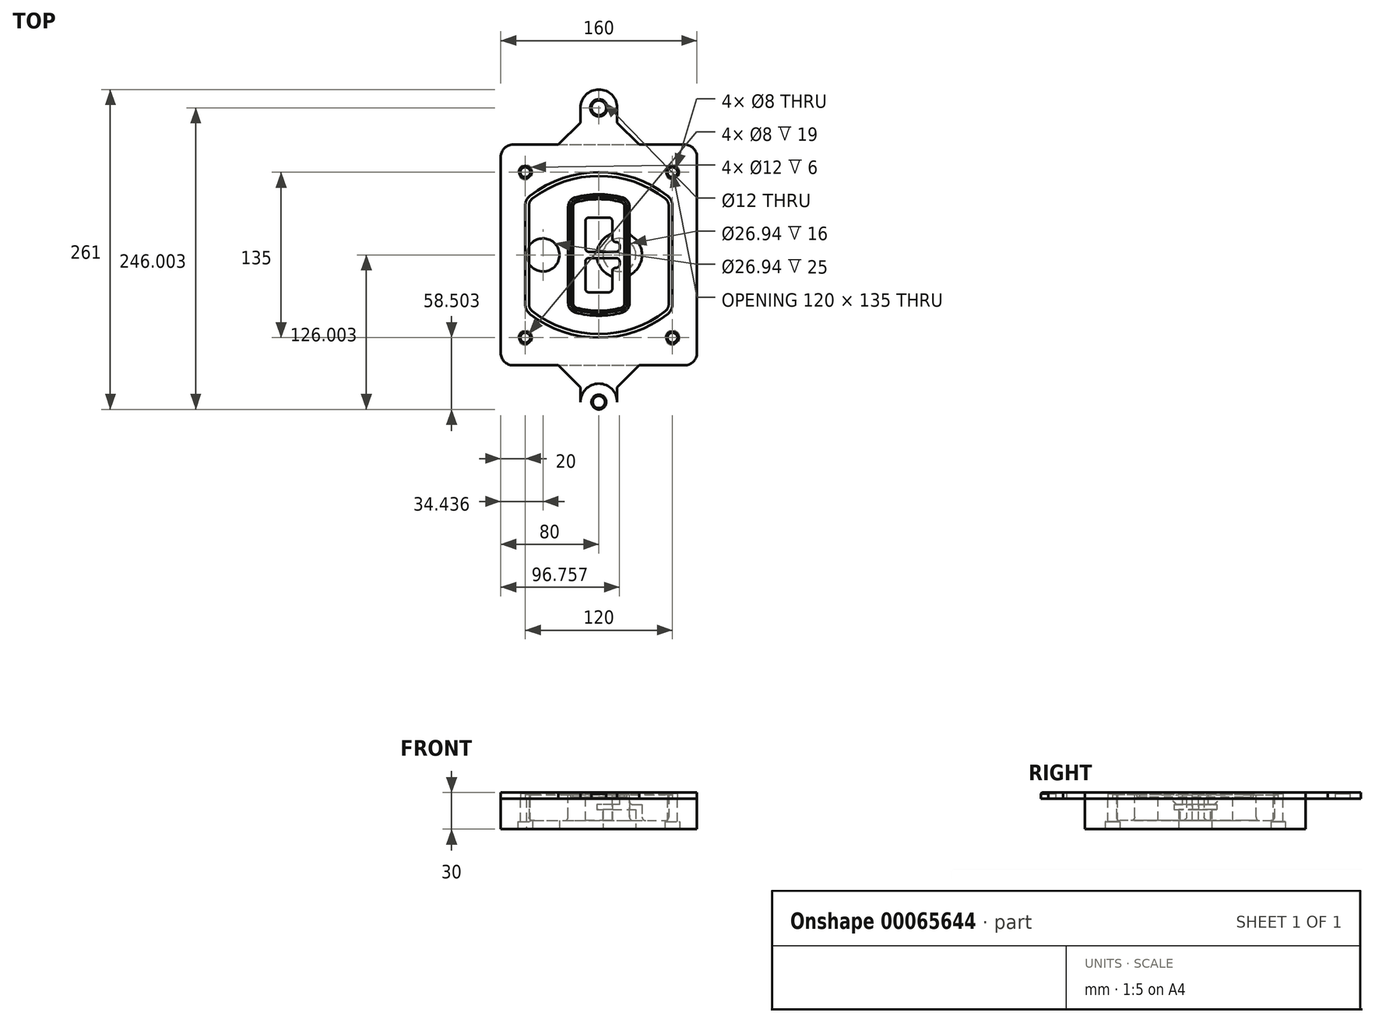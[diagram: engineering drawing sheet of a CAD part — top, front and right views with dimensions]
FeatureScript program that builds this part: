
annotation { "Feature Type Name" : "Feature", "Feature Type Description" : "" }
export const myFeature = defineFeature(function(context is Context, id is Id, definition is map)
    precondition{}
    {
        {
            var Q0;
            Q0=qCreatedBy(makeId("Top.planeOp"),FACE);
            var sketch = newSketch(context, id + "F0", { "sketchPlane" : qUnion([Q0])});
            skPoint(sketch, "E0.rect.middle", {"position": v(0, 0) * mm});
            skLineSegment(sketch, "E1.bottom", {"start": v(24.05, 28.38) * mm, "end": v(164.05, 28.38) * mm});
            skLineSegment(sketch, "E1.top", {"start": v(24.05, 208.38) * mm, "end": v(164.05, 208.38) * mm});
            skLineSegment(sketch, "E1.left", {"start": v(14.05, 38.38) * mm, "end": v(14.05, 198.38) * mm});
            skLineSegment(sketch, "E1.right", {"start": v(174.05, 38.38) * mm, "end": v(174.05, 198.38) * mm});
            skLineSegment(sketch, "E2", {"start": v(14.05, 208.38) * mm, "end": v(174.05, 28.38) * mm, "construction": true});
            skLineSegment(sketch, "E3", {"start": v(174.05, 208.38) * mm, "end": v(14.05, 28.38) * mm, "construction": true});
            skCircle(sketch, "E4", {"center": v(34.05, 185.88) * mm, "radius": 4 * mm});
            skCircle(sketch, "E5", {"center": v(154.05, 185.88) * mm, "radius": 4 * mm});
            skCircle(sketch, "E6", {"center": v(154.05, 50.88) * mm, "radius": 4 * mm});
            skCircle(sketch, "E7", {"center": v(34.05, 50.88) * mm, "radius": 4 * mm});
            skLineSegment(sketch, "E8", {"start": v(34.05, 185.88) * mm, "end": v(154.05, 185.88) * mm, "construction": true});
            skLineSegment(sketch, "E9", {"start": v(154.05, 185.88) * mm, "end": v(154.05, 50.88) * mm, "construction": true});
            skLineSegment(sketch, "E10", {"start": v(154.05, 50.88) * mm, "end": v(34.05, 50.88) * mm, "construction": true});
            skLineSegment(sketch, "E11", {"start": v(34.05, 50.88) * mm, "end": v(34.05, 185.88) * mm, "construction": true});
            skLineSegment(sketch, "E12", {"start": v(34.05, 158.68) * mm, "end": v(34.05, 78.09) * mm});
            skLineSegment(sketch, "E13", {"start": v(154.05, 158.68) * mm, "end": v(154.05, 78.09) * mm});
            skArc(sketch, "E14", {"start": v(150.2, 166.56) * mm, "mid": v(94.05, 185.88) * mm, "end": v(37.9, 166.56) * mm});
            skArc(sketch, "E15", {"start": v(37.9, 70.2) * mm, "mid": v(94.05, 50.88) * mm, "end": v(150.2, 70.2) * mm});
            skLineSegment(sketch, "E16", {"start": v(34.05, 118.38) * mm, "end": v(154.05, 118.38) * mm, "construction": true});
            skPoint(sketch, "E17.visualSharp", {"position": v(34.05, 73.38) * mm});
            skArc(sketch, "E17.filletArc", {"start": v(34.05, 78.09) * mm, "mid": v(35.06, 73.7) * mm, "end": v(37.9, 70.2) * mm});
            skPoint(sketch, "E18.visualSharp", {"position": v(34.05, 163.38) * mm});
            skArc(sketch, "E18.filletArc", {"start": v(37.9, 166.56) * mm, "mid": v(35.06, 163.06) * mm, "end": v(34.05, 158.68) * mm});
            skPoint(sketch, "E19.visualSharp", {"position": v(154.05, 163.38) * mm});
            skArc(sketch, "E19.filletArc", {"start": v(154.05, 158.68) * mm, "mid": v(153.04, 163.06) * mm, "end": v(150.2, 166.56) * mm});
            skPoint(sketch, "E20.visualSharp", {"position": v(154.05, 73.38) * mm});
            skArc(sketch, "E20.filletArc", {"start": v(150.2, 70.2) * mm, "mid": v(153.04, 73.7) * mm, "end": v(154.05, 78.09) * mm});
            skPoint(sketch, "E21.visualSharp", {"position": v(14.05, 208.38) * mm});
            skArc(sketch, "E21.filletArc", {"start": v(24.05, 208.38) * mm, "mid": v(16.98, 205.45) * mm, "end": v(14.05, 198.38) * mm});
            skPoint(sketch, "E22.visualSharp", {"position": v(174.05, 208.38) * mm});
            skArc(sketch, "E22.filletArc", {"start": v(174.05, 198.38) * mm, "mid": v(171.12, 205.45) * mm, "end": v(164.05, 208.38) * mm});
            skPoint(sketch, "E23.visualSharp", {"position": v(174.05, 28.38) * mm});
            skArc(sketch, "E23.filletArc", {"start": v(164.05, 28.38) * mm, "mid": v(171.12, 31.31) * mm, "end": v(174.05, 38.38) * mm});
            skPoint(sketch, "E24.visualSharp", {"position": v(14.05, 28.38) * mm});
            skArc(sketch, "E24.filletArc", {"start": v(14.05, 38.38) * mm, "mid": v(16.98, 31.31) * mm, "end": v(24.05, 28.38) * mm});
            skArc(sketch, "E25.0", {"start": v(151.05, 158.68) * mm, "mid": v(150.34, 161.75) * mm, "end": v(148.36, 164.2) * mm});
            skLineSegment(sketch, "E25.1", {"start": v(151.05, 158.68) * mm, "end": v(151.05, 78.09) * mm});
            skArc(sketch, "E25.2", {"start": v(148.36, 72.57) * mm, "mid": v(150.34, 75.02) * mm, "end": v(151.05, 78.09) * mm});
            skArc(sketch, "E25.3", {"start": v(39.74, 72.57) * mm, "mid": v(94.05, 53.88) * mm, "end": v(148.36, 72.57) * mm});
            skArc(sketch, "E25.4", {"start": v(37.05, 78.09) * mm, "mid": v(37.76, 75.02) * mm, "end": v(39.74, 72.57) * mm});
            skArc(sketch, "E25.5", {"start": v(148.36, 164.2) * mm, "mid": v(94.05, 182.88) * mm, "end": v(39.74, 164.2) * mm});
            skLineSegment(sketch, "E25.6", {"start": v(37.05, 158.68) * mm, "end": v(37.05, 78.09) * mm});
            skArc(sketch, "E25.7", {"start": v(39.74, 164.2) * mm, "mid": v(37.76, 161.75) * mm, "end": v(37.05, 158.68) * mm});
            skArc(sketch, "E26.0", {"start": v(35.43, 169.71) * mm, "mid": v(31.47, 164.82) * mm, "end": v(30.05, 158.68) * mm});
            skArc(sketch, "E26.1", {"start": v(152.67, 169.71) * mm, "mid": v(94.05, 189.88) * mm, "end": v(35.43, 169.71) * mm});
            skArc(sketch, "E26.2", {"start": v(158.05, 158.68) * mm, "mid": v(156.63, 164.82) * mm, "end": v(152.67, 169.71) * mm});
            skLineSegment(sketch, "E26.3", {"start": v(158.05, 158.68) * mm, "end": v(158.05, 78.09) * mm});
            skArc(sketch, "E26.4", {"start": v(152.67, 67.05) * mm, "mid": v(156.63, 71.95) * mm, "end": v(158.05, 78.09) * mm});
            skLineSegment(sketch, "E26.5", {"start": v(30.05, 158.68) * mm, "end": v(30.05, 78.09) * mm});
            skArc(sketch, "E26.6", {"start": v(35.43, 67.05) * mm, "mid": v(94.05, 46.88) * mm, "end": v(152.67, 67.05) * mm});
            skArc(sketch, "E26.7", {"start": v(30.05, 78.09) * mm, "mid": v(31.47, 71.95) * mm, "end": v(35.43, 67.05) * mm});
            skSolve(sketch);
        }
        {
            var Q0;
            Q0=makeQuery(id+"F0.imprint","IMPRINT",FACE,{"disambiguationData":[TD([[makeQuery(id+"F0.imprint","IMPRINT",EDGE,{"derivedFrom":sQuery(id+"F0.wireOp",EDGE,"E1.bottom")}),1.0]])]});
            var Q1;
            Q1=makeQuery(id+"F0.imprint","IMPRINT",FACE,{"disambiguationData":[TD([[makeQuery(id+"F0.imprint","IMPRINT",EDGE,{"derivedFrom":sQuery(id+"F0.wireOp",EDGE,"E12")}),1.0]])]});
            var Q2;
            Q2=makeQuery(id+"F0.imprint","IMPRINT",FACE,{"disambiguationData":[TD([[makeQuery(id+"F0.imprint","IMPRINT",EDGE,{"derivedFrom":sQuery(id+"F0.wireOp",EDGE,"E25.0")}),1.0]])]});
            var Q3;
            Q3=makeQuery(id+"F0.imprint","IMPRINT",FACE,{"disambiguationData":[TD([[makeQuery(id+"F0.imprint","IMPRINT",EDGE,{"derivedFrom":sQuery(id+"F0.wireOp",EDGE,"E12")}),-1.0]])]});
            extrude(context, id + "F1", {"entities" : qUnion([Q0, Q1, Q2, Q3]), "oppositeDirection" : true, "depth" : 25 * mm});
        }
        {
            var Q0;
            Q0=makeQuery(id+"F0.imprint","IMPRINT",FACE,{"disambiguationData":[TD([[makeQuery(id+"F0.imprint","IMPRINT",EDGE,{"derivedFrom":sQuery(id+"F0.wireOp",EDGE,"E12")}),1.0]])]});
            extrude(context, id + "F2", {"entities" : qUnion([Q0]), "operationType" : NewBodyOperationType.ADD, "depth" : 3 * mm});
        }
        {
            var Q0;
            Q0=makeQuery(id+"F0.imprint","IMPRINT",FACE,{"disambiguationData":[TD([[makeQuery(id+"F0.imprint","IMPRINT",EDGE,{"derivedFrom":sQuery(id+"F0.wireOp",EDGE,"E25.0")}),1.0]])]});
            extrude(context, id + "F3", {"entities" : qUnion([Q0]), "operationType" : NewBodyOperationType.REMOVE, "oppositeDirection" : true, "depth" : 18 * mm});
        }
        {
            var Q0;
            Q0=makeQuery(id+"F2.opExtrude","CAP_FACE",FACE,{"disambiguationData":[OSD([sQuery(id+"F0.wireOp",EDGE,"E12"),sQuery(id+"F0.wireOp",EDGE,"E13"),sQuery(id+"F0.wireOp",EDGE,"E14"),sQuery(id+"F0.wireOp",EDGE,"E15"),sQuery(id+"F0.wireOp",EDGE,"E17.filletArc"),sQuery(id+"F0.wireOp",EDGE,"E18.filletArc"),sQuery(id+"F0.wireOp",EDGE,"E19.filletArc"),sQuery(id+"F0.wireOp",EDGE,"E20.filletArc"),sQuery(id+"F0.wireOp",EDGE,"E25.0"),sQuery(id+"F0.wireOp",EDGE,"E25.1"),sQuery(id+"F0.wireOp",EDGE,"E25.2"),sQuery(id+"F0.wireOp",EDGE,"E25.3"),sQuery(id+"F0.wireOp",EDGE,"E25.4"),sQuery(id+"F0.wireOp",EDGE,"E25.5"),sQuery(id+"F0.wireOp",EDGE,"E25.6"),sQuery(id+"F0.wireOp",EDGE,"E25.7")])],"isStart":false});
            var sketch = newSketch(context, id + "F4", { "sketchPlane" : qUnion([Q0])});
            skArc(sketch, "E27.0", {"start": v(74.97, 71.41) * mm, "mid": v(94.05, 68.88) * mm, "end": v(113.13, 71.41) * mm});
            skArc(sketch, "E28.0", {"start": v(113.13, 165.35) * mm, "mid": v(94.05, 167.88) * mm, "end": v(74.97, 165.35) * mm});
            skLineSegment(sketch, "E29", {"start": v(69.05, 157.63) * mm, "end": v(69.05, 79.14) * mm});
            skLineSegment(sketch, "E30", {"start": v(119.05, 157.63) * mm, "end": v(119.05, 79.14) * mm});
            skLineSegment(sketch, "E31", {"start": v(69.05, 163.48) * mm, "end": v(119.05, 163.48) * mm, "construction": true});
            skLineSegment(sketch, "E32", {"start": v(69.05, 73.28) * mm, "end": v(119.05, 73.28) * mm, "construction": true});
            skPoint(sketch, "E33.visualSharp", {"position": v(69.05, 163.48) * mm});
            skArc(sketch, "E33.filletArc", {"start": v(74.97, 165.35) * mm, "mid": v(70.7, 162.5) * mm, "end": v(69.05, 157.63) * mm});
            skPoint(sketch, "E34.visualSharp", {"position": v(119.05, 163.48) * mm});
            skArc(sketch, "E34.filletArc", {"start": v(119.05, 157.63) * mm, "mid": v(117.4, 162.5) * mm, "end": v(113.13, 165.35) * mm});
            skPoint(sketch, "E35.visualSharp", {"position": v(119.05, 73.28) * mm});
            skArc(sketch, "E35.filletArc", {"start": v(113.13, 71.41) * mm, "mid": v(117.4, 74.27) * mm, "end": v(119.05, 79.14) * mm});
            skPoint(sketch, "E36.visualSharp", {"position": v(69.05, 73.28) * mm});
            skArc(sketch, "E36.filletArc", {"start": v(69.05, 79.14) * mm, "mid": v(70.7, 74.27) * mm, "end": v(74.97, 71.41) * mm});
            skArc(sketch, "E37.0", {"start": v(148.36, 164.2) * mm, "mid": v(94.05, 182.88) * mm, "end": v(39.74, 164.2) * mm});
            skArc(sketch, "E37.1", {"start": v(39.74, 164.2) * mm, "mid": v(37.76, 161.75) * mm, "end": v(37.05, 158.68) * mm});
            skLineSegment(sketch, "E37.2", {"start": v(37.05, 158.68) * mm, "end": v(37.05, 78.09) * mm});
            skArc(sketch, "E37.3", {"start": v(37.05, 78.09) * mm, "mid": v(37.76, 75.02) * mm, "end": v(39.74, 72.57) * mm});
            skArc(sketch, "E37.4", {"start": v(39.74, 72.57) * mm, "mid": v(94.05, 53.88) * mm, "end": v(148.36, 72.57) * mm});
            skArc(sketch, "E37.5", {"start": v(148.36, 72.57) * mm, "mid": v(150.34, 75.02) * mm, "end": v(151.05, 78.09) * mm});
            skLineSegment(sketch, "E37.6", {"start": v(151.05, 158.68) * mm, "end": v(151.05, 78.09) * mm});
            skArc(sketch, "E37.7", {"start": v(151.05, 158.68) * mm, "mid": v(150.34, 161.75) * mm, "end": v(148.36, 164.2) * mm});
            skLineSegment(sketch, "E38.0", {"start": v(117.05, 157.63) * mm, "end": v(117.05, 79.14) * mm});
            skArc(sketch, "E38.1", {"start": v(112.61, 73.34) * mm, "mid": v(115.81, 75.49) * mm, "end": v(117.05, 79.14) * mm});
            skArc(sketch, "E38.2", {"start": v(75.49, 73.34) * mm, "mid": v(94.05, 70.88) * mm, "end": v(112.61, 73.34) * mm});
            skArc(sketch, "E38.3", {"start": v(71.05, 79.14) * mm, "mid": v(72.29, 75.49) * mm, "end": v(75.49, 73.34) * mm});
            skLineSegment(sketch, "E38.4", {"start": v(71.05, 157.63) * mm, "end": v(71.05, 79.14) * mm});
            skArc(sketch, "E38.5", {"start": v(117.05, 157.63) * mm, "mid": v(115.81, 161.28) * mm, "end": v(112.61, 163.42) * mm});
            skArc(sketch, "E38.6", {"start": v(75.49, 163.42) * mm, "mid": v(72.29, 161.28) * mm, "end": v(71.05, 157.63) * mm});
            skArc(sketch, "E38.7", {"start": v(112.61, 163.42) * mm, "mid": v(94.05, 165.88) * mm, "end": v(75.49, 163.42) * mm});
            skArc(sketch, "E39.0", {"start": v(115.05, 157.63) * mm, "mid": v(114.23, 160.06) * mm, "end": v(112.1, 161.5) * mm});
            skLineSegment(sketch, "E39.1", {"start": v(115.05, 157.63) * mm, "end": v(115.05, 79.14) * mm});
            skArc(sketch, "E39.2", {"start": v(112.1, 75.27) * mm, "mid": v(114.23, 76.7) * mm, "end": v(115.05, 79.14) * mm});
            skArc(sketch, "E39.3", {"start": v(76, 75.27) * mm, "mid": v(94.05, 72.88) * mm, "end": v(112.1, 75.27) * mm});
            skArc(sketch, "E39.4", {"start": v(73.05, 79.14) * mm, "mid": v(73.87, 76.7) * mm, "end": v(76, 75.27) * mm});
            skArc(sketch, "E39.5", {"start": v(112.1, 161.5) * mm, "mid": v(94.05, 163.88) * mm, "end": v(76, 161.5) * mm});
            skLineSegment(sketch, "E39.6", {"start": v(73.05, 157.63) * mm, "end": v(73.05, 79.14) * mm});
            skArc(sketch, "E39.7", {"start": v(76, 161.5) * mm, "mid": v(73.87, 160.06) * mm, "end": v(73.05, 157.63) * mm});
            skLineSegment(sketch, "E40", {"start": v(69.05, 118.38) * mm, "end": v(119.05, 118.38) * mm, "construction": true});
            skLineSegment(sketch, "E41", {"start": v(83.05, 123.88) * mm, "end": v(83.05, 145.88) * mm});
            skLineSegment(sketch, "E42", {"start": v(86.05, 148.88) * mm, "end": v(102.05, 148.88) * mm});
            skLineSegment(sketch, "E43", {"start": v(105.05, 145.88) * mm, "end": v(105.05, 131.88) * mm});
            skLineSegment(sketch, "E44", {"start": v(108.05, 128.88) * mm, "end": v(108.05, 128.88) * mm});
            skLineSegment(sketch, "E45", {"start": v(111.05, 125.88) * mm, "end": v(111.05, 123.88) * mm});
            skLineSegment(sketch, "E46", {"start": v(108.05, 120.88) * mm, "end": v(86.05, 120.88) * mm});
            skPoint(sketch, "E47.visualSharp", {"position": v(83.05, 148.88) * mm});
            skArc(sketch, "E47.filletArc", {"start": v(86.05, 148.88) * mm, "mid": v(83.93, 148) * mm, "end": v(83.05, 145.88) * mm});
            skPoint(sketch, "E48.visualSharp", {"position": v(105.05, 148.88) * mm});
            skArc(sketch, "E48.filletArc", {"start": v(105.05, 145.88) * mm, "mid": v(104.17, 148) * mm, "end": v(102.05, 148.88) * mm});
            skPoint(sketch, "E49.visualSharp", {"position": v(105.05, 128.88) * mm});
            skArc(sketch, "E49.filletArc", {"start": v(105.05, 131.88) * mm, "mid": v(105.93, 129.76) * mm, "end": v(108.05, 128.88) * mm});
            skPoint(sketch, "E50.visualSharp", {"position": v(111.05, 128.88) * mm});
            skArc(sketch, "E50.filletArc", {"start": v(111.05, 125.88) * mm, "mid": v(110.17, 128) * mm, "end": v(108.05, 128.88) * mm});
            skPoint(sketch, "E51.visualSharp", {"position": v(111.05, 120.88) * mm});
            skArc(sketch, "E51.filletArc", {"start": v(108.05, 120.88) * mm, "mid": v(110.17, 121.76) * mm, "end": v(111.05, 123.88) * mm});
            skPoint(sketch, "E52.visualSharp", {"position": v(83.05, 120.88) * mm});
            skArc(sketch, "E52.filletArc", {"start": v(83.05, 123.88) * mm, "mid": v(83.93, 121.76) * mm, "end": v(86.05, 120.88) * mm});
            skLineSegment(sketch, "E53.0.MirrorCS", {"start": v(108.05, 115.88) * mm, "end": v(86.05, 115.88) * mm});
            skArc(sketch, "E54.0.MirrorCS", {"start": v(83.05, 112.88) * mm, "mid": v(83.93, 115) * mm, "end": v(86.05, 115.88) * mm});
            skLineSegment(sketch, "E55.0.MirrorCS", {"start": v(83.05, 112.88) * mm, "end": v(83.05, 90.88) * mm});
            skArc(sketch, "E56.0.MirrorCS", {"start": v(86.05, 87.88) * mm, "mid": v(83.93, 88.76) * mm, "end": v(83.05, 90.88) * mm});
            skLineSegment(sketch, "E57.0.MirrorCS", {"start": v(86.05, 87.88) * mm, "end": v(102.05, 87.88) * mm});
            skArc(sketch, "E58.0.MirrorCS", {"start": v(105.05, 90.88) * mm, "mid": v(104.17, 88.76) * mm, "end": v(102.05, 87.88) * mm});
            skLineSegment(sketch, "E59.0.MirrorCS", {"start": v(105.05, 90.88) * mm, "end": v(105.05, 104.88) * mm});
            skArc(sketch, "E60.0.MirrorCS", {"start": v(105.05, 104.88) * mm, "mid": v(105.93, 107) * mm, "end": v(108.05, 107.88) * mm});
            skArc(sketch, "E61.0.MirrorCS", {"start": v(111.05, 110.88) * mm, "mid": v(110.17, 108.76) * mm, "end": v(108.05, 107.88) * mm});
            skLineSegment(sketch, "E62.0.MirrorCS", {"start": v(111.05, 110.88) * mm, "end": v(111.05, 112.88) * mm});
            skArc(sketch, "E63.0.MirrorCS", {"start": v(108.05, 115.88) * mm, "mid": v(110.17, 115) * mm, "end": v(111.05, 112.88) * mm});
            skSolve(sketch);
        }
        {
            var Q0;
            Q0=makeQuery(id+"F4.imprint","IMPRINT",FACE,{"disambiguationData":[TD([[makeQuery(id+"F4.imprint","IMPRINT",EDGE,{"derivedFrom":sQuery(id+"F4.wireOp",EDGE,"E27.0")}),1.0]])]});
            var Q1;
            Q1=makeQuery(id+"F4.imprint","IMPRINT",FACE,{"disambiguationData":[TD([[makeQuery(id+"F4.imprint","IMPRINT",EDGE,{"derivedFrom":sQuery(id+"F4.wireOp",EDGE,"E38.0")}),-1.0]])]});
            var Q2;
            Q2=makeQuery(id+"F4.imprint","IMPRINT",FACE,{"disambiguationData":[TD([[makeQuery(id+"F4.imprint","IMPRINT",EDGE,{"derivedFrom":sQuery(id+"F4.wireOp",EDGE,"E39.0")}),1.0]])]});
            extrude(context, id + "F5", {"entities" : qUnion([Q0, Q1, Q2]), "operationType" : NewBodyOperationType.ADD, "endBound" : BoundingType.UP_TO_NEXT, "oppositeDirection" : true, "depth" : 25 * mm});
        }
        {
            var Q0;
            Q0=makeQuery(id+"F4.imprint","IMPRINT",FACE,{"disambiguationData":[TD([[makeQuery(id+"F4.imprint","IMPRINT",EDGE,{"derivedFrom":sQuery(id+"F4.wireOp",EDGE,"E38.0")}),-1.0]])]});
            extrude(context, id + "F6", {"entities" : qUnion([Q0]), "operationType" : NewBodyOperationType.REMOVE, "oppositeDirection" : true, "depth" : 2 * mm});
        }
        {
            var Q0;
            Q0=makeQuery(id+"F1.opExtrude","CAP_FACE",FACE,{"disambiguationData":[OSD([sQuery(id+"F0.wireOp",EDGE,"E1.bottom"),sQuery(id+"F0.wireOp",EDGE,"E1.top"),sQuery(id+"F0.wireOp",EDGE,"E1.left"),sQuery(id+"F0.wireOp",EDGE,"E1.right"),sQuery(id+"F0.wireOp",EDGE,"E4"),sQuery(id+"F0.wireOp",EDGE,"E5"),sQuery(id+"F0.wireOp",EDGE,"E6"),sQuery(id+"F0.wireOp",EDGE,"E7"),sQuery(id+"F0.wireOp",EDGE,"E21.filletArc"),sQuery(id+"F0.wireOp",EDGE,"E22.filletArc"),sQuery(id+"F0.wireOp",EDGE,"E23.filletArc"),sQuery(id+"F0.wireOp",EDGE,"E24.filletArc")])],"isStart":false});
            var sketch = newSketch(context, id + "F7", { "sketchPlane" : qUnion([Q0])});
            skCircle(sketch, "E64", {"center": v(110.8, -118.38) * mm, "radius": 13.47 * mm});
            skCircle(sketch, "E65", {"center": v(48.49, -118.38) * mm, "radius": 13.47 * mm});
            skLineSegment(sketch, "E66", {"start": v(174.05, -118.38) * mm, "end": v(14.05, -118.38) * mm});
            skCircle(sketch, "E67", {"center": v(110.8, -118.38) * mm, "radius": 18.47 * mm});
            skCircle(sketch, "E68", {"center": v(154.05, -185.88) * mm, "radius": 6 * mm});
            skCircle(sketch, "E69", {"center": v(34.05, -185.88) * mm, "radius": 6 * mm});
            skCircle(sketch, "E70", {"center": v(34.05, -50.88) * mm, "radius": 6 * mm});
            skCircle(sketch, "E71", {"center": v(154.05, -50.88) * mm, "radius": 6 * mm});
            skSolve(sketch);
        }
        {
            var Q0;
            {var subQ1=sQuery(id+"F7.wireOp",EDGE,"E66");var subQ4=sQuery(id+"F7.wireOp",EDGE,"E64");var subQ6=makeQuery(id+"F7.imprint","INTERSECT",VERTEX,{"disambiguationData":[OD(0.0)],"derivedFrom":[subQ4,subQ1]});Q0=makeQuery(id+"F7.imprint","IMPRINT",FACE,{"disambiguationData":[TD([[makeQuery(id+"F7.imprint","IMPRINT",EDGE,{"disambiguationData":[TD([[subQ6,-1.0]])],"derivedFrom":subQ4}),-1.0]])]});}
            var Q1;
            {var subQ0=sQuery(id+"F7.wireOp",EDGE,"E66");var subQ1=sQuery(id+"F7.wireOp",EDGE,"E64");var subQ3=makeQuery(id+"F7.imprint","INTERSECT",VERTEX,{"disambiguationData":[OD(0.0)],"derivedFrom":[subQ1,subQ0]});Q1=makeQuery(id+"F7.imprint","IMPRINT",FACE,{"disambiguationData":[TD([[makeQuery(id+"F7.imprint","IMPRINT",EDGE,{"disambiguationData":[TD([[subQ3,-1.0]])],"derivedFrom":subQ1}),1.0]])]});}
            var Q2;
            {var subQ0=sQuery(id+"F7.wireOp",EDGE,"E66");var subQ1=sQuery(id+"F7.wireOp",EDGE,"E64");var subQ3=makeQuery(id+"F7.imprint","INTERSECT",VERTEX,{"disambiguationData":[OD(0.0)],"derivedFrom":[subQ1,subQ0]});Q2=makeQuery(id+"F7.imprint","IMPRINT",FACE,{"disambiguationData":[TD([[makeQuery(id+"F7.imprint","IMPRINT",EDGE,{"disambiguationData":[TD([[subQ3,1.0]])],"derivedFrom":subQ1}),1.0]])]});}
            var Q3;
            {var subQ1=sQuery(id+"F7.wireOp",EDGE,"E66");var subQ4=sQuery(id+"F7.wireOp",EDGE,"E64");var subQ6=makeQuery(id+"F7.imprint","INTERSECT",VERTEX,{"disambiguationData":[OD(0.0)],"derivedFrom":[subQ4,subQ1]});Q3=makeQuery(id+"F7.imprint","IMPRINT",FACE,{"disambiguationData":[TD([[makeQuery(id+"F7.imprint","IMPRINT",EDGE,{"disambiguationData":[TD([[subQ6,1.0]])],"derivedFrom":subQ4}),-1.0]])]});}
            extrude(context, id + "F8", {"entities" : qUnion([Q0, Q1, Q2, Q3]), "operationType" : NewBodyOperationType.ADD, "oppositeDirection" : true, "depth" : 20 * mm});
        }
        {
            var Q0;
            {var subQ0=sQuery(id+"F7.wireOp",EDGE,"E66");var subQ1=sQuery(id+"F7.wireOp",EDGE,"E64");var subQ3=makeQuery(id+"F7.imprint","INTERSECT",VERTEX,{"disambiguationData":[OD(0.0)],"derivedFrom":[subQ1,subQ0]});Q0=makeQuery(id+"F7.imprint","IMPRINT",FACE,{"disambiguationData":[TD([[makeQuery(id+"F7.imprint","IMPRINT",EDGE,{"disambiguationData":[TD([[subQ3,-1.0]])],"derivedFrom":subQ1}),1.0]])]});}
            var Q1;
            {var subQ0=sQuery(id+"F7.wireOp",EDGE,"E66");var subQ1=sQuery(id+"F7.wireOp",EDGE,"E64");var subQ3=makeQuery(id+"F7.imprint","INTERSECT",VERTEX,{"disambiguationData":[OD(0.0)],"derivedFrom":[subQ1,subQ0]});Q1=makeQuery(id+"F7.imprint","IMPRINT",FACE,{"disambiguationData":[TD([[makeQuery(id+"F7.imprint","IMPRINT",EDGE,{"disambiguationData":[TD([[subQ3,1.0]])],"derivedFrom":subQ1}),1.0]])]});}
            extrude(context, id + "F9", {"entities" : qUnion([Q0, Q1]), "operationType" : NewBodyOperationType.REMOVE, "oppositeDirection" : true, "depth" : 16 * mm});
        }
        {
            var Q0;
            {var subQ0=sQuery(id+"F7.wireOp",EDGE,"E66");var subQ1=sQuery(id+"F7.wireOp",EDGE,"E65");var subQ3=makeQuery(id+"F7.imprint","INTERSECT",VERTEX,{"disambiguationData":[OD(0.0)],"derivedFrom":[subQ1,subQ0]});Q0=makeQuery(id+"F7.imprint","IMPRINT",FACE,{"disambiguationData":[TD([[makeQuery(id+"F7.imprint","IMPRINT",EDGE,{"disambiguationData":[TD([[subQ3,-1.0]])],"derivedFrom":subQ1}),1.0]])]});}
            var Q1;
            {var subQ0=sQuery(id+"F7.wireOp",EDGE,"E66");var subQ1=sQuery(id+"F7.wireOp",EDGE,"E65");var subQ3=makeQuery(id+"F7.imprint","INTERSECT",VERTEX,{"disambiguationData":[OD(0.0)],"derivedFrom":[subQ1,subQ0]});Q1=makeQuery(id+"F7.imprint","IMPRINT",FACE,{"disambiguationData":[TD([[makeQuery(id+"F7.imprint","IMPRINT",EDGE,{"disambiguationData":[TD([[subQ3,1.0]])],"derivedFrom":subQ1}),1.0]])]});}
            extrude(context, id + "F10", {"entities" : qUnion([Q0, Q1]), "operationType" : NewBodyOperationType.REMOVE, "oppositeDirection" : true, "depth" : 25 * mm});
        }
        {
            var Q0;
            Q0=makeQuery(id+"F7.imprint","IMPRINT",FACE,{"disambiguationData":[TD([[makeQuery(id+"F7.imprint","IMPRINT",EDGE,{"derivedFrom":sQuery(id+"F7.wireOp",EDGE,"E68")}),1.0]])]});
            var Q1;
            Q1=makeQuery(id+"F7.imprint","IMPRINT",FACE,{"disambiguationData":[TD([[makeQuery(id+"F7.imprint","IMPRINT",EDGE,{"derivedFrom":makeQuery(id+"F1.opExtrude","CAP_EDGE",EDGE,{"disambiguationData":[OSD([sQuery(id+"F0.wireOp",EDGE,"E5")])],"isStart":false})}),-1.0]])]});
            var Q2;
            Q2=makeQuery(id+"F7.imprint","IMPRINT",FACE,{"disambiguationData":[TD([[makeQuery(id+"F7.imprint","IMPRINT",EDGE,{"derivedFrom":sQuery(id+"F7.wireOp",EDGE,"E69")}),1.0]])]});
            var Q3;
            Q3=makeQuery(id+"F7.imprint","IMPRINT",FACE,{"disambiguationData":[TD([[makeQuery(id+"F7.imprint","IMPRINT",EDGE,{"derivedFrom":makeQuery(id+"F1.opExtrude","CAP_EDGE",EDGE,{"disambiguationData":[OSD([sQuery(id+"F0.wireOp",EDGE,"E4")])],"isStart":false})}),-1.0]])]});
            var Q4;
            Q4=makeQuery(id+"F7.imprint","IMPRINT",FACE,{"disambiguationData":[TD([[makeQuery(id+"F7.imprint","IMPRINT",EDGE,{"derivedFrom":sQuery(id+"F7.wireOp",EDGE,"E70")}),1.0]])]});
            var Q5;
            Q5=makeQuery(id+"F7.imprint","IMPRINT",FACE,{"disambiguationData":[TD([[makeQuery(id+"F7.imprint","IMPRINT",EDGE,{"derivedFrom":makeQuery(id+"F1.opExtrude","CAP_EDGE",EDGE,{"disambiguationData":[OSD([sQuery(id+"F0.wireOp",EDGE,"E7")])],"isStart":false})}),-1.0]])]});
            var Q6;
            Q6=makeQuery(id+"F7.imprint","IMPRINT",FACE,{"disambiguationData":[TD([[makeQuery(id+"F7.imprint","IMPRINT",EDGE,{"derivedFrom":sQuery(id+"F7.wireOp",EDGE,"E71")}),1.0]])]});
            var Q7;
            Q7=makeQuery(id+"F7.imprint","IMPRINT",FACE,{"disambiguationData":[TD([[makeQuery(id+"F7.imprint","IMPRINT",EDGE,{"derivedFrom":makeQuery(id+"F1.opExtrude","CAP_EDGE",EDGE,{"disambiguationData":[OSD([sQuery(id+"F0.wireOp",EDGE,"E6")])],"isStart":false})}),-1.0]])]});
            extrude(context, id + "F11", {"entities" : qUnion([Q0, Q1, Q2, Q3, Q4, Q5, Q6, Q7]), "operationType" : NewBodyOperationType.REMOVE, "oppositeDirection" : true, "depth" : 6 * mm});
        }
        {
            var Q0;
            Q0=makeQuery(id+"F9.boolean.opBoolean","COPY",FACE,{"derivedFrom":makeQuery(id+"F9.opExtrude","CAP_FACE",FACE,{"disambiguationData":[OSD([sQuery(id+"F7.wireOp",EDGE,"E64")])],"isStart":false})});
            var sketch = newSketch(context, id + "F12", { "sketchPlane" : qUnion([Q0])});
            skArc(sketch, "E72.0", {"start": v(105.05, -100.83) * mm, "mid": v(96.62, -106.56) * mm, "end": v(92.5, -115.88) * mm});
            skArc(sketch, "E72.1", {"start": v(92.5, -120.88) * mm, "mid": v(96.62, -130.2) * mm, "end": v(105.05, -135.93) * mm});
            skLineSegment(sketch, "E73", {"start": v(92.5, -120.88) * mm, "end": v(108.05, -120.88) * mm});
            skLineSegment(sketch, "E74.0", {"start": v(108.05, -115.88) * mm, "end": v(92.5, -115.88) * mm});
            skArc(sketch, "E74.1", {"start": v(108.05, -115.88) * mm, "mid": v(110.17, -115) * mm, "end": v(111.05, -112.88) * mm});
            skLineSegment(sketch, "E74.2", {"start": v(111.05, -110.88) * mm, "end": v(111.05, -112.88) * mm});
            skArc(sketch, "E74.3", {"start": v(111.05, -110.88) * mm, "mid": v(110.17, -108.76) * mm, "end": v(108.05, -107.88) * mm});
            skArc(sketch, "E74.4", {"start": v(105.05, -104.88) * mm, "mid": v(105.93, -107) * mm, "end": v(108.05, -107.88) * mm});
            skLineSegment(sketch, "E74.5", {"start": v(105.05, -100.83) * mm, "end": v(105.05, -104.88) * mm});
            skLineSegment(sketch, "E74.7", {"start": v(108.05, -120.88) * mm, "end": v(92.5, -120.88) * mm});
            skArc(sketch, "E74.8", {"start": v(108.05, -120.88) * mm, "mid": v(110.17, -121.76) * mm, "end": v(111.05, -123.88) * mm});
            skLineSegment(sketch, "E74.9", {"start": v(111.05, -125.88) * mm, "end": v(111.05, -123.88) * mm});
            skArc(sketch, "E74.10", {"start": v(111.05, -125.88) * mm, "mid": v(110.17, -128) * mm, "end": v(108.05, -128.88) * mm});
            skArc(sketch, "E74.11", {"start": v(105.05, -131.88) * mm, "mid": v(105.93, -129.76) * mm, "end": v(108.05, -128.88) * mm});
            skLineSegment(sketch, "E74.12", {"start": v(105.05, -135.93) * mm, "end": v(105.05, -131.88) * mm});
            skPoint(sketch, "E75.orphan", {"position": v(105.05, -145.88) * mm});
            skPoint(sketch, "E76.orphan", {"position": v(86.05, -120.88) * mm});
            skPoint(sketch, "E77.orphan", {"position": v(86.05, -115.88) * mm});
            skPoint(sketch, "E78.orphan", {"position": v(105.05, -90.88) * mm});
            skSolve(sketch);
        }
        {
            var Q0;
            {var subQ7=sQuery(id+"F12.wireOp",EDGE,"E72.0");var subQ14=sQuery(id+"F12.wireOp",EDGE,"E72.1");var subQ16=sQuery(id+"F12.wireOp",EDGE,"E74.1");var subQ18=sQuery(id+"F12.wireOp",EDGE,"E74.8");Q0=qUnion([makeQuery(id+"F12.imprint","IMPRINT",FACE,{"disambiguationData":[TD([[makeQuery(id+"F12.imprint","IMPRINT",EDGE,{"derivedFrom":subQ7}),1.0]])]}),makeQuery(id+"F12.imprint","IMPRINT",FACE,{"disambiguationData":[TD([[makeQuery(id+"F12.imprint","IMPRINT",EDGE,{"derivedFrom":subQ14}),1.0]])]}),makeQuery(id+"F12.imprint","IMPRINT",FACE,{"disambiguationData":[TD([[makeQuery(id+"F12.imprint","IMPRINT",EDGE,{"derivedFrom":subQ16}),1.0]])]}),makeQuery(id+"F12.imprint","IMPRINT",FACE,{"disambiguationData":[TD([[makeQuery(id+"F12.imprint","IMPRINT",EDGE,{"derivedFrom":subQ18}),-1.0]])]})]);}
            var Q1;
            Q1=makeQuery(id+"F5.boolean.opBoolean","SPLIT",FACE,{"disambiguationData":[TD([makeQuery(id+"F5.opExtrude","SWEPT_FACE",FACE,{"disambiguationData":[OSD([sQuery(id+"F4.wireOp",EDGE,"E41")])]})])],"derivedFrom":makeQuery(id+"F3.boolean.opBoolean","COPY",FACE,{"derivedFrom":makeQuery(id+"F3.opExtrude","CAP_FACE",FACE,{"disambiguationData":[OSD([sQuery(id+"F0.wireOp",EDGE,"E25.0"),sQuery(id+"F0.wireOp",EDGE,"E25.1"),sQuery(id+"F0.wireOp",EDGE,"E25.2"),sQuery(id+"F0.wireOp",EDGE,"E25.3"),sQuery(id+"F0.wireOp",EDGE,"E25.4"),sQuery(id+"F0.wireOp",EDGE,"E25.5"),sQuery(id+"F0.wireOp",EDGE,"E25.6"),sQuery(id+"F0.wireOp",EDGE,"E25.7")])],"isStart":false})})});
            extrude(context, id + "F13", {"entities" : qUnion([Q0]), "operationType" : NewBodyOperationType.REMOVE, "endBound" : BoundingType.UP_TO_SURFACE, "endBoundEntityFace" : qUnion([Q1]), "depth" : 25 * mm});
        }
        {
            var Q0;
            Q0=makeQuery(id+"F3.boolean.opBoolean","COPY",EDGE,{"derivedFrom":makeQuery(id+"F3.opExtrude","CAP_EDGE",EDGE,{"disambiguationData":[OSD([sQuery(id+"F0.wireOp",EDGE,"E25.6")])],"isStart":false})});
            var Q1;
            Q1=makeQuery(id+"F8.boolean.opBoolean","INTERSECT",EDGE,{"derivedFrom":[makeQuery(id+"F5.opExtrude","SWEPT_FACE",FACE,{"disambiguationData":[OSD([sQuery(id+"F4.wireOp",EDGE,"E30")])]}),makeQuery(id+"F8.opExtrude","CAP_FACE",FACE,{"disambiguationData":[OSD([sQuery(id+"F7.wireOp",EDGE,"E67")])],"isStart":false})]});
            var Q2;
            Q2=makeQuery(id+"F8.boolean.opBoolean","INTERSECT",EDGE,{"disambiguationData":[OD(1.0)],"derivedFrom":[makeQuery(id+"F5.opExtrude","SWEPT_FACE",FACE,{"disambiguationData":[OSD([sQuery(id+"F4.wireOp",EDGE,"E30")])]}),makeQuery(id+"F8.opExtrude","SWEPT_FACE",FACE,{"disambiguationData":[OSD([sQuery(id+"F7.wireOp",EDGE,"E67")])]})]});
            var Q3;
            {var subQ0=sQuery(id+"F4.wireOp",EDGE,"E30");Q3=makeQuery(id+"F8.boolean.opBoolean","SPLIT",EDGE,{"disambiguationData":[TD([makeQuery(id+"F5.opExtrude","SWEPT_FACE",FACE,{"disambiguationData":[OSD([sQuery(id+"F4.wireOp",EDGE,"E35.filletArc")])]})])],"derivedFrom":makeQuery(id+"F5.opExtrude","CAP_EDGE",EDGE,{"disambiguationData":[OSD([subQ0])],"isStart":false})});}
            var Q4;
            {var subQ0=sQuery(id+"F0.wireOp",EDGE,"E25.7");var subQ1=sQuery(id+"F0.wireOp",EDGE,"E25.1");var subQ2=sQuery(id+"F0.wireOp",EDGE,"E25.6");var subQ3=sQuery(id+"F0.wireOp",EDGE,"E25.5");var subQ4=sQuery(id+"F0.wireOp",EDGE,"E25.4");var subQ5=sQuery(id+"F0.wireOp",EDGE,"E25.0");var subQ6=sQuery(id+"F0.wireOp",EDGE,"E25.2");var subQ7=sQuery(id+"F0.wireOp",EDGE,"E25.3");Q4=makeQuery(id+"F8.boolean.opBoolean","INTERSECT",EDGE,{"derivedFrom":[makeQuery(id+"F5.boolean.opBoolean","SPLIT",FACE,{"disambiguationData":[TD([makeQuery(id+"F2.opExtrude","SWEPT_FACE",FACE,{"disambiguationData":[OSD([subQ5])]})])],"derivedFrom":makeQuery(id+"F3.boolean.opBoolean","COPY",FACE,{"derivedFrom":makeQuery(id+"F3.opExtrude","CAP_FACE",FACE,{"disambiguationData":[OSD([subQ5,subQ1,subQ6,subQ7,subQ4,subQ3,subQ2,subQ0])],"isStart":false})})}),makeQuery(id+"F8.opExtrude","SWEPT_FACE",FACE,{"disambiguationData":[OSD([sQuery(id+"F7.wireOp",EDGE,"E67")])]})]});}
            var Q5;
            Q5=makeQuery(id+"F8.boolean.opBoolean","INTERSECT",EDGE,{"disambiguationData":[OD(0.0)],"derivedFrom":[makeQuery(id+"F5.opExtrude","SWEPT_FACE",FACE,{"disambiguationData":[OSD([sQuery(id+"F4.wireOp",EDGE,"E30")])]}),makeQuery(id+"F8.opExtrude","SWEPT_FACE",FACE,{"disambiguationData":[OSD([sQuery(id+"F7.wireOp",EDGE,"E67")])]})]});
            fillet(context, id + "F14", {"entities" : qUnion([Q0, Q1, Q2, Q3, Q4, Q5]), "radius" : 3 * mm, "tangentPropagation" : true, "allowEdgeOverflow" : false});
        }
        {
            var Q0;
            {var subQ0=sQuery(id+"F0.wireOp",EDGE,"E22.filletArc");var subQ1=sQuery(id+"F0.wireOp",EDGE,"E7");var subQ2=sQuery(id+"F0.wireOp",EDGE,"E6");var subQ3=sQuery(id+"F0.wireOp",EDGE,"E5");var subQ4=sQuery(id+"F0.wireOp",EDGE,"E4");var subQ5=sQuery(id+"F0.wireOp",EDGE,"E1.bottom");var subQ6=sQuery(id+"F0.wireOp",EDGE,"E21.filletArc");var subQ7=sQuery(id+"F0.wireOp",EDGE,"E1.top");var subQ8=sQuery(id+"F0.wireOp",EDGE,"E1.left");var subQ9=sQuery(id+"F0.wireOp",EDGE,"E1.right");var subQ10=sQuery(id+"F0.wireOp",EDGE,"E23.filletArc");var subQ11=sQuery(id+"F0.wireOp",EDGE,"E24.filletArc");Q0=makeQuery(id+"F2.boolean.opBoolean","SPLIT",FACE,{"disambiguationData":[TD([makeQuery(id+"F1.opExtrude","SWEPT_FACE",FACE,{"disambiguationData":[OSD([subQ5])]})])],"derivedFrom":makeQuery(id+"F1.opExtrude","CAP_FACE",FACE,{"disambiguationData":[OSD([subQ5,subQ7,subQ8,subQ9,subQ4,subQ3,subQ2,subQ1,subQ6,subQ0,subQ10,subQ11])],"isStart":true})});}
            var sketch = newSketch(context, id + "F15", { "sketchPlane" : qUnion([Q0])});
            skLineSegment(sketch, "E79", {"start": v(61.05, 208.38) * mm, "end": v(79.05, 226.38) * mm});
            skLineSegment(sketch, "E80", {"start": v(109.05, 226.38) * mm, "end": v(127.05, 208.38) * mm});
            skLineSegment(sketch, "E81", {"start": v(94.05, 208.38) * mm, "end": v(94.05, 238.38) * mm, "construction": true});
            skCircle(sketch, "E82", {"center": v(94.05, 238.38) * mm, "radius": 6 * mm});
            skCircle(sketch, "E83", {"center": v(94.05, 238.38) * mm, "radius": 15 * mm});
            skLineSegment(sketch, "E84", {"start": v(79.05, 226.38) * mm, "end": v(79.05, 238.38) * mm});
            skLineSegment(sketch, "E85", {"start": v(109.05, 226.38) * mm, "end": v(109.05, 238.38) * mm});
            skLineSegment(sketch, "E86", {"start": v(14.05, 118.38) * mm, "end": v(174.05, 118.38) * mm, "construction": true});
            skLineSegment(sketch, "E87.MirrorCS", {"start": v(94.05, 28.38) * mm, "end": v(94.05, -1.62) * mm, "construction": true});
            skCircle(sketch, "E88.MirrorC", {"center": v(94.05, -1.62) * mm, "radius": 6 * mm});
            skLineSegment(sketch, "E89.MirrorCS", {"start": v(109.05, 10.38) * mm, "end": v(109.05, -1.62) * mm});
            skLineSegment(sketch, "E90.MirrorCS", {"start": v(79.05, 10.38) * mm, "end": v(79.05, -1.62) * mm});
            skCircle(sketch, "E91.MirrorC", {"center": v(94.05, -1.62) * mm, "radius": 15 * mm});
            skLineSegment(sketch, "E92.MirrorCS", {"start": v(61.05, 28.38) * mm, "end": v(79.05, 10.38) * mm});
            skLineSegment(sketch, "E93.MirrorCS", {"start": v(109.05, 10.38) * mm, "end": v(127.05, 28.38) * mm});
            skSolve(sketch);
        }
        {
            var Q0;
            Q0=makeQuery(id+"F15.imprint","IMPRINT",FACE,{"disambiguationData":[TD([[makeQuery(id+"F15.imprint","IMPRINT",EDGE,{"derivedFrom":sQuery(id+"F15.wireOp",EDGE,"E82")}),-1.0]])]});
            var Q1;
            {var subQ4=sQuery(id+"F15.wireOp",EDGE,"E79");Q1=makeQuery(id+"F15.imprint","IMPRINT",FACE,{"disambiguationData":[TD([[makeQuery(id+"F15.imprint","IMPRINT",EDGE,{"derivedFrom":subQ4}),-1.0]])]});}
            var Q2;
            Q2=makeQuery(id+"F15.imprint","IMPRINT",FACE,{"disambiguationData":[TD([[makeQuery(id+"F15.imprint","IMPRINT",EDGE,{"derivedFrom":makeQuery(id+"F1.opExtrude","CAP_EDGE",EDGE,{"disambiguationData":[OSD([sQuery(id+"F0.wireOp",EDGE,"E1.left")])],"isStart":true})}),-1.0]])]});
            var Q3;
            {var subQ1=sQuery(id+"F15.wireOp",EDGE,"E89.MirrorCS");Q3=makeQuery(id+"F15.imprint","IMPRINT",FACE,{"disambiguationData":[TD([[makeQuery(id+"F15.imprint","IMPRINT",EDGE,{"derivedFrom":subQ1}),-1.0]])]});}
            var Q4;
            Q4=makeQuery(id+"F15.imprint","IMPRINT",FACE,{"disambiguationData":[TD([[makeQuery(id+"F15.imprint","IMPRINT",EDGE,{"derivedFrom":sQuery(id+"F15.wireOp",EDGE,"E88.MirrorC")}),1.0]])]});
            extrude(context, id + "F16", {"entities" : qUnion([Q0, Q1, Q2, Q3, Q4]), "depth" : 5 * mm});
        }
        {
            var Q0;
            Q0=makeQuery(id+"F16.opExtrude","CAP_EDGE",EDGE,{"disambiguationData":[OSD([sQuery(id+"F0.wireOp",EDGE,"E6")])],"isStart":false});
            var Q1;
            Q1=makeQuery(id+"F16.opExtrude","CAP_EDGE",EDGE,{"disambiguationData":[OSD([sQuery(id+"F0.wireOp",EDGE,"E7")])],"isStart":false});
            var Q2;
            Q2=makeQuery(id+"F16.opExtrude","CAP_EDGE",EDGE,{"disambiguationData":[OSD([sQuery(id+"F0.wireOp",EDGE,"E4")])],"isStart":false});
            var Q3;
            Q3=makeQuery(id+"F16.opExtrude","CAP_EDGE",EDGE,{"disambiguationData":[OSD([sQuery(id+"F0.wireOp",EDGE,"E5")])],"isStart":false});
            var Q4;
            Q4=makeQuery(id+"F16.opExtrude","CAP_EDGE",EDGE,{"disambiguationData":[OSD([sQuery(id+"F15.wireOp",EDGE,"E88.MirrorC")])],"isStart":false});
            var Q5;
            Q5=makeQuery(id+"F16.opExtrude","CAP_EDGE",EDGE,{"disambiguationData":[OSD([sQuery(id+"F15.wireOp",EDGE,"E82")])],"isStart":false});
            chamfer(context, id + "F17", {"entities" : qUnion([Q0, Q1, Q2, Q3, Q4, Q5]), "width" : 1 * mm});
        }
    });
